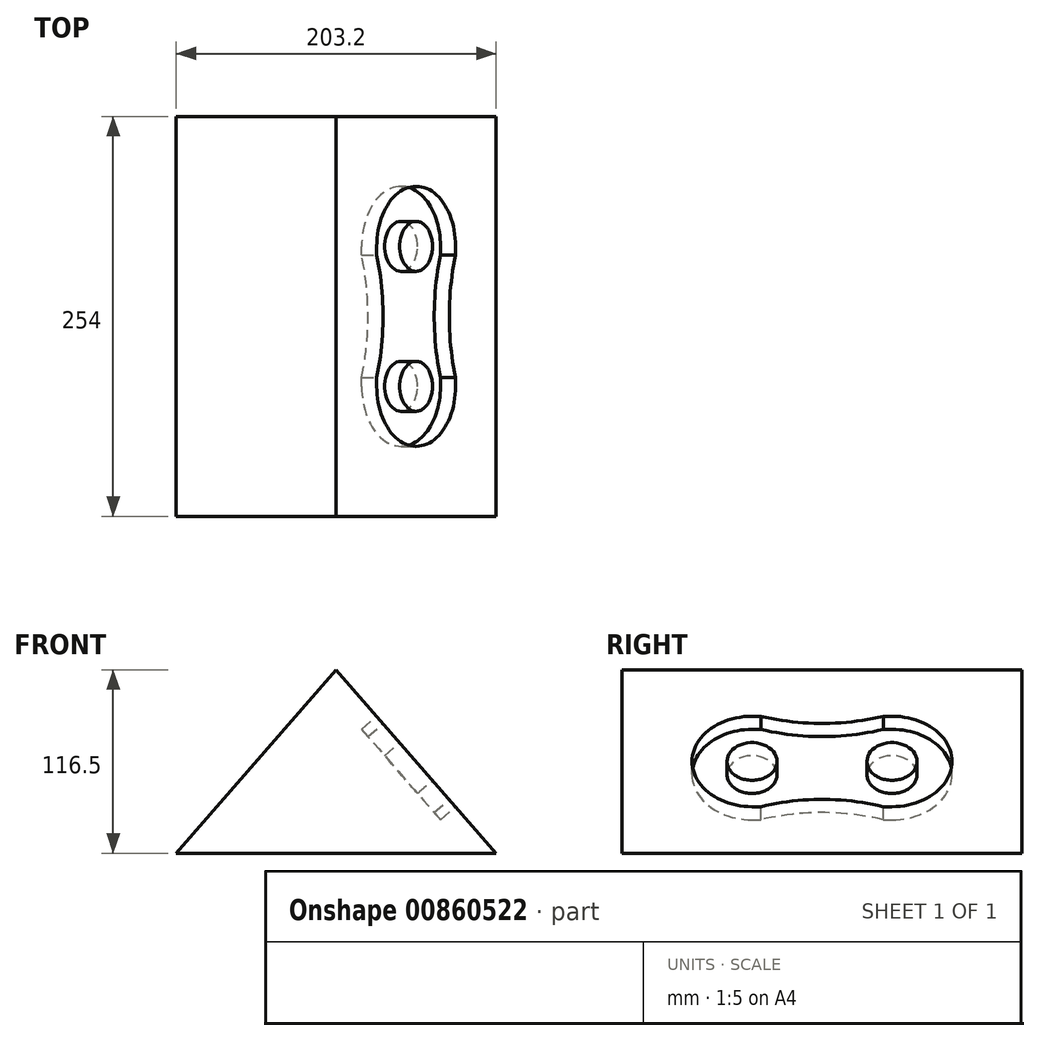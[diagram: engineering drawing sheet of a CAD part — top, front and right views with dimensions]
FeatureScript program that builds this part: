
annotation { "Feature Type Name" : "Feature", "Feature Type Description" : "" }
export const myFeature = defineFeature(function(context is Context, id is Id, definition is map)
    precondition{}
    {
        {
            var Q0;
            Q0=qCreatedBy(makeId("Front.planeOp"),FACE);
            var sketch = newSketch(context, id + "F0", { "sketchPlane" : qUnion([Q0])});
            skLineSegment(sketch, "E0", {"start": v(0, 0) * mm, "end": v(203.2, 0) * mm});
            skLineSegment(sketch, "E1", {"start": v(0, 0) * mm, "end": v(101.6, 116.5) * mm});
            skLineSegment(sketch, "E2", {"start": v(101.6, 116.5) * mm, "end": v(203.2, 0) * mm});
            skLineSegment(sketch, "E3", {"start": v(101.6, 0) * mm, "end": v(101.6, 169.46) * mm, "construction": true});
            skSolve(sketch);
        }
        {
            var Q0;
            Q0=makeQuery(id+"F0.imprint","IMPRINT",FACE,{"disambiguationData":[TD([[makeQuery(id+"F0.imprint","IMPRINT",EDGE,{"derivedFrom":sQuery(id+"F0.wireOp",EDGE,"E0")}),1.0]])]});
            extrude(context, id + "F1", {"entities" : qUnion([Q0]), "depth" : 254 * mm, "offsetDistance" : 25.4 * mm});
        }
        {
            var Q0;
            Q0=makeQuery(id+"F1.opExtrude","SWEPT_FACE",FACE,{"disambiguationData":[OSD([sQuery(id+"F0.wireOp",EDGE,"E2")])]});
            var sketch = newSketch(context, id + "F2", { "sketchPlane" : qUnion([Q0])});
            skArc(sketch, "E4", {"start": v(-171.45, -18.17) * mm, "mid": v(-209.55, -56.27) * mm, "end": v(-171.45, -94.37) * mm});
            skArc(sketch, "E5", {"start": v(-82.55, -94.37) * mm, "mid": v(-44.45, -56.27) * mm, "end": v(-82.55, -18.17) * mm});
            skLineSegment(sketch, "E6", {"start": v(-254, -56.27) * mm, "end": v(0, -56.27) * mm, "construction": true});
            skLineSegment(sketch, "E7", {"start": v(-171.45, -18.17) * mm, "end": v(-165.88, -18.17) * mm});
            skLineSegment(sketch, "E8.0", {"start": v(-171.45, -94.37) * mm, "end": v(-165.88, -94.37) * mm});
            skArc(sketch, "E9", {"start": v(-165.88, -18.17) * mm, "mid": v(-127, -24.26) * mm, "end": v(-88.12, -18.17) * mm});
            skArc(sketch, "E10.MirrorC", {"start": v(-165.88, -94.37) * mm, "mid": v(-127, -88.27) * mm, "end": v(-88.12, -94.37) * mm});
            skLineSegment(sketch, "E11.trimOffspring", {"start": v(-88.12, -18.17) * mm, "end": v(-82.55, -18.17) * mm});
            skLineSegment(sketch, "E12.trimOffspring", {"start": v(-88.12, -94.37) * mm, "end": v(-82.55, -94.37) * mm});
            skCircle(sketch, "E13", {"center": v(-171.45, -56.27) * mm, "radius": 15.88 * mm});
            skCircle(sketch, "E14", {"center": v(-82.55, -56.27) * mm, "radius": 15.88 * mm});
            skSolve(sketch);
        }
        {
            var Q0;
            Q0=makeQuery(id+"F2.imprint","IMPRINT",FACE,{"disambiguationData":[TD([[makeQuery(id+"F2.imprint","IMPRINT",EDGE,{"derivedFrom":sQuery(id+"F2.wireOp",EDGE,"E4")}),1.0]])]});
            extrude(context, id + "F3", {"entities" : qUnion([Q0]), "operationType" : NewBodyOperationType.REMOVE, "oppositeDirection" : true, "depth" : 12.7 * mm, "offsetDistance" : 25.4 * mm});
        }
        {
            var Q0;
            Q0=qCreatedBy(makeId("Right.planeOp"),FACE);
            cPlane(context, id + "F4", {"entities" : qUnion([Q0]), "cplaneType" : CPlaneType.OFFSET, "offset" : 101.6 * mm, "width" : 152.4 * mm, "height" : 152.4 * mm});
        }
    });
